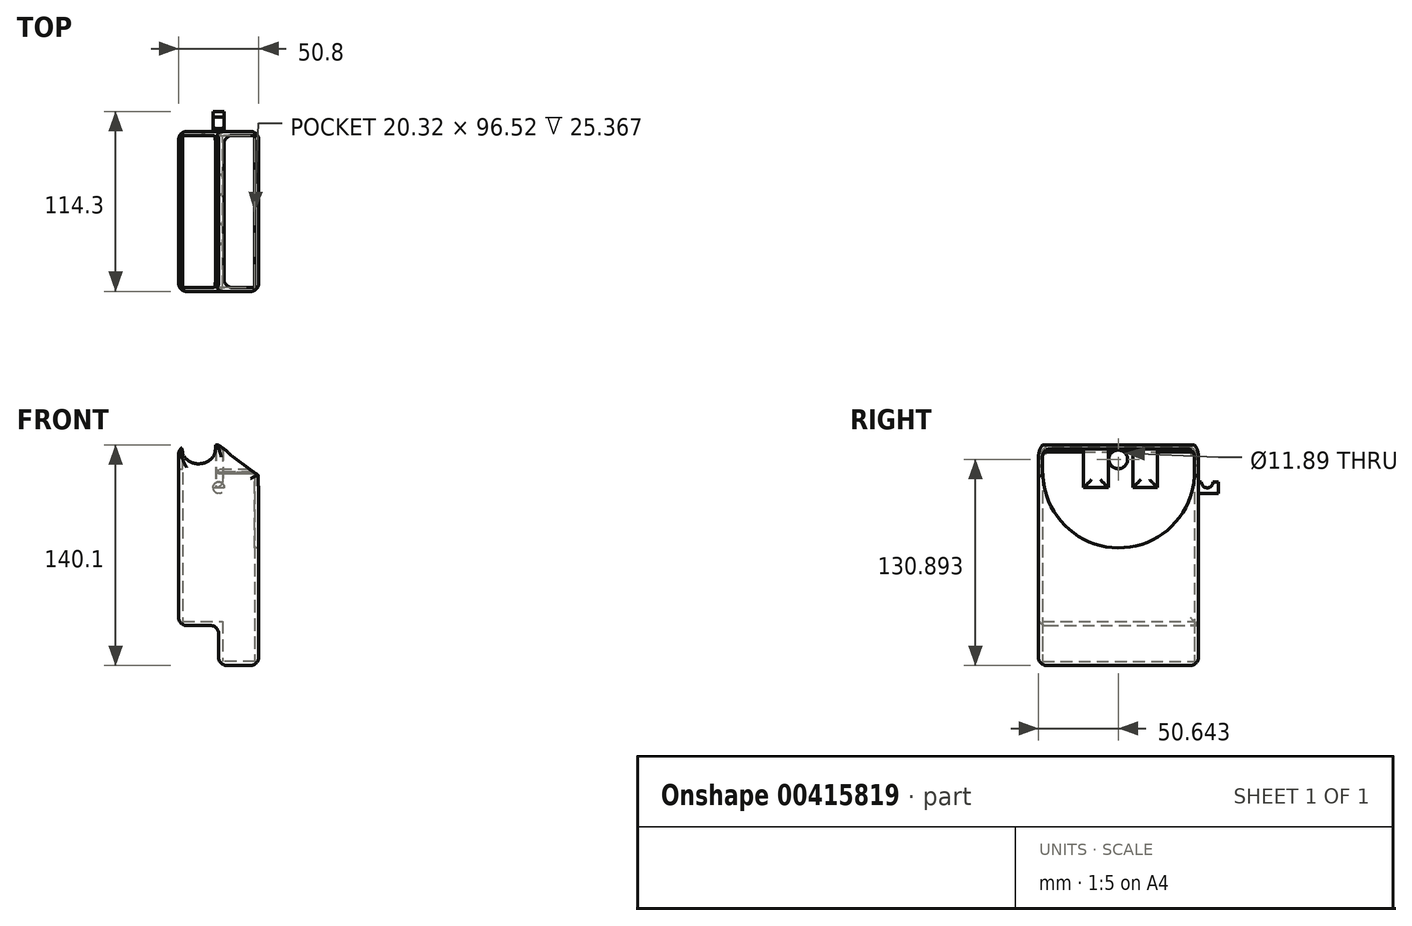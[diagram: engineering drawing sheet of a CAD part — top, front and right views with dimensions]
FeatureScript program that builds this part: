
annotation { "Feature Type Name" : "Feature", "Feature Type Description" : "" }
export const myFeature = defineFeature(function(context is Context, id is Id, definition is map)
    precondition{}
    {
        {
            var Q0;
            Q0=qCreatedBy(makeId("Front.planeOp"),FACE);
            var sketch = newSketch(context, id + "F0", { "sketchPlane" : qUnion([Q0])});
            skLineSegment(sketch, "E0", {"start": v(-25.4, 26.25) * mm, "end": v(-25.4, -87.62) * mm});
            skLineSegment(sketch, "E1", {"start": v(-25.4, -87.62) * mm, "end": v(0, -87.62) * mm});
            skLineSegment(sketch, "E2", {"start": v(0, 27.1) * mm, "end": v(0, -87.23) * mm});
            skLineSegment(sketch, "E3", {"start": v(25.4, -87.23) * mm, "end": v(25.4, 8.36) * mm});
            skLineSegment(sketch, "E4", {"start": v(0, 27.1) * mm, "end": v(25.4, 8.36) * mm});
            skLineSegment(sketch, "E5", {"start": v(-25.4, 26.25) * mm, "end": v(-23.58, 26.31) * mm});
            skArc(sketch, "E6", {"start": v(-23.58, 26.31) * mm, "mid": v(-12.33, 15.8) * mm, "end": v(-1.82, 27.05) * mm});
            skLineSegment(sketch, "E7.trimOffspring", {"start": v(-1.82, 27.05) * mm, "end": v(0, 27.1) * mm});
            skLineSegment(sketch, "E8", {"start": v(0, -87.23) * mm, "end": v(0, -112.99) * mm});
            skLineSegment(sketch, "E9", {"start": v(25.4, -87.23) * mm, "end": v(25.4, -112.99) * mm});
            skLineSegment(sketch, "E10", {"start": v(25.4, -112.99) * mm, "end": v(0, -112.99) * mm});
            skSolve(sketch);
        }
        {
            var Q0;
            Q0 = qSketchRegion(id + "F0", true);
            extrude(context, id + "F1", {"entities" : qUnion([Q0]), "depth" : 101.6 * mm});
        }
        {
            var Q0;
            Q0=makeQuery(id+"F1.opExtrude","SWEPT_FACE",FACE,{"disambiguationData":[OSD([sQuery(id+"F0.wireOp",EDGE,"E4")])]});
            var Q1;
            Q1=makeQuery(id+"F1.opExtrude","SWEPT_FACE",FACE,{"disambiguationData":[OSD([sQuery(id+"F0.wireOp",EDGE,"E6")])]});
            shell(context, id + "F2", {"entities" : qUnion([Q0, Q1]), "thickness" : 2.54 * mm});
        }
        {
            var Q0;
            Q0=qCreatedBy(makeId("Right.planeOp"),FACE);
            var sketch = newSketch(context, id + "F3", { "sketchPlane" : qUnion([Q0])});
            skArc(sketch, "E11", {"start": v(-98.82, 9.51) * mm, "mid": v(-50.48, -38.25) * mm, "end": v(-2.52, 9.9) * mm});
            skLineSegment(sketch, "E12", {"start": v(-98.82, 9.51) * mm, "end": v(-50.67, 9.9) * mm});
            skLineSegment(sketch, "E13", {"start": v(-2.52, 9.9) * mm, "end": v(-50.67, 9.9) * mm});
            skSolve(sketch);
        }
        {
            var Q0;
            Q0 = qSketchRegion(id + "F3", true);
            extrude(context, id + "F4", {"entities" : qUnion([Q0]), "operationType" : NewBodyOperationType.REMOVE, "depth" : 25.4 * mm});
        }
        {
            var Q0;
            Q0=qCreatedBy(makeId("Right.planeOp"),FACE);
            var sketch = newSketch(context, id + "F5", { "sketchPlane" : qUnion([Q0])});
            skCircle(sketch, "E14", {"center": v(-50.96, 17.9) * mm, "radius": 5.95 * mm});
            skSolve(sketch);
        }
        {
            var Q0;
            Q0 = qSketchRegion(id + "F5", true);
            extrude(context, id + "F6", {"entities" : qUnion([Q0]), "operationType" : NewBodyOperationType.REMOVE, "oppositeDirection" : true, "depth" : 25.4 * mm});
        }
        {
            var Q0;
            Q0=qCreatedBy(makeId("Front.planeOp"),FACE);
            var sketch = newSketch(context, id + "F7", { "sketchPlane" : qUnion([Q0])});
            skCircle(sketch, "E15", {"center": v(0, 0) * mm, "radius": 3.57 * mm});
            skSolve(sketch);
        }
        {
            var Q0;
            Q0 = qSketchRegion(id + "F7", true);
            extrude(context, id + "F8", {"entities" : qUnion([Q0]), "operationType" : NewBodyOperationType.ADD, "oppositeDirection" : true, "depth" : 12.7 * mm});
        }
        {
            var Q0;
            Q0=qCreatedBy(makeId("Right.planeOp"),FACE);
            var sketch = newSketch(context, id + "F9", { "sketchPlane" : qUnion([Q0])});
            skCircle(sketch, "E16", {"center": v(5.6, 3.45) * mm, "radius": 3.64 * mm});
            skSolve(sketch);
        }
        {
            var Q0;
            Q0 = qSketchRegion(id + "F9", true);
            extrude(context, id + "F10", {"entities" : qUnion([Q0]), "operationType" : NewBodyOperationType.REMOVE, "endBound" : BoundingType.SYMMETRIC, "depth" : 25.4 * mm});
        }
        {
            var Q0;
            Q0=makeQuery(id+"F1.opExtrude","CAP_EDGE",EDGE,{"disambiguationData":[OSD([sQuery(id+"F0.wireOp",EDGE,"E0")])],"isStart":true});
            var Q1;
            Q1=makeQuery(id+"F1.opExtrude","SWEPT_EDGE",EDGE,{"disambiguationData":[OSD([sQuery(id+"F0.wireOp",EDGE,"E0"),sQuery(id+"F0.wireOp",EDGE,"E1")])]});
            var Q2;
            Q2=makeQuery(id+"F1.opExtrude","CAP_EDGE",EDGE,{"disambiguationData":[OSD([sQuery(id+"F0.wireOp",EDGE,"E0")])],"isStart":false});
            var Q3;
            Q3=makeQuery(id+"F1.opExtrude","CAP_EDGE",EDGE,{"disambiguationData":[OSD([sQuery(id+"F0.wireOp",EDGE,"E1")])],"isStart":false});
            var Q4;
            Q4=makeQuery(id+"F1.opExtrude","CAP_EDGE",EDGE,{"disambiguationData":[OSD([sQuery(id+"F0.wireOp",EDGE,"E8")])],"isStart":false});
            var Q5;
            Q5=makeQuery(id+"F1.opExtrude","SWEPT_EDGE",EDGE,{"disambiguationData":[OSD([sQuery(id+"F0.wireOp",EDGE,"E8"),sQuery(id+"F0.wireOp",EDGE,"E10")])]});
            var Q6;
            Q6=makeQuery(id+"F1.opExtrude","SWEPT_FACE",FACE,{"disambiguationData":[OSD([sQuery(id+"F0.wireOp",EDGE,"E8")])]});
            var Q7;
            Q7=makeQuery(id+"F1.opExtrude","CAP_EDGE",EDGE,{"disambiguationData":[OSD([sQuery(id+"F0.wireOp",EDGE,"E10")])],"isStart":true});
            var Q8;
            Q8=makeQuery(id+"F1.opExtrude","CAP_EDGE",EDGE,{"disambiguationData":[OSD([sQuery(id+"F0.wireOp",EDGE,"E3"),sQuery(id+"F0.wireOp",EDGE,"E9")])],"isStart":true});
            var Q9;
            Q9=makeQuery(id+"F1.opExtrude","SWEPT_EDGE",EDGE,{"disambiguationData":[OSD([sQuery(id+"F0.wireOp",EDGE,"E9"),sQuery(id+"F0.wireOp",EDGE,"E10")])]});
            var Q10;
            Q10=makeQuery(id+"F1.opExtrude","CAP_EDGE",EDGE,{"disambiguationData":[OSD([sQuery(id+"F0.wireOp",EDGE,"E3"),sQuery(id+"F0.wireOp",EDGE,"E9")])],"isStart":false});
            var Q11;
            Q11=makeQuery(id+"F1.opExtrude","CAP_EDGE",EDGE,{"disambiguationData":[OSD([sQuery(id+"F0.wireOp",EDGE,"E10")])],"isStart":false});
            var Q12;
            Q12=makeQuery(id+"F1.opExtrude","CAP_EDGE",EDGE,{"disambiguationData":[OSD([sQuery(id+"F0.wireOp",EDGE,"E6")])],"isStart":true});
            var Q13;
            Q13=makeQuery(id+"F1.opExtrude","CAP_EDGE",EDGE,{"disambiguationData":[OSD([sQuery(id+"F0.wireOp",EDGE,"E6")])],"isStart":false});
            var Q14;
            Q14=makeQuery(id+"F1.opExtrude","CAP_EDGE",EDGE,{"disambiguationData":[OSD([sQuery(id+"F0.wireOp",EDGE,"E4")])],"isStart":false});
            fillet(context, id + "F11", {"entities" : qUnion([Q0, Q1, Q2, Q3, Q4, Q5, Q6, Q7, Q8, Q9, Q10, Q11, Q12, Q13, Q14]), "radius" : 5.08 * mm, "tangentPropagation" : true, "allowEdgeOverflow" : false});
        }
        {
            var Q0;
            Q0=qCreatedBy(makeId("Right.planeOp"),FACE);
            var sketch = newSketch(context, id + "F12", { "sketchPlane" : qUnion([Q0])});
            skLineSegment(sketch, "E17.bottom", {"start": v(-98.06, 11.65) * mm, "end": v(-2.9, 11.65) * mm});
            skLineSegment(sketch, "E17.top", {"start": v(-98.06, 9) * mm, "end": v(-2.9, 9) * mm});
            skLineSegment(sketch, "E17.right", {"start": v(-2.9, 11.65) * mm, "end": v(-2.9, 9) * mm});
            skLineSegment(sketch, "E18.bottom", {"start": v(-98.06, 9) * mm, "end": v(-99.13, 9) * mm});
            skLineSegment(sketch, "E18.top", {"start": v(-98.06, 11.65) * mm, "end": v(-99.13, 11.65) * mm});
            skLineSegment(sketch, "E18.right", {"start": v(-99.13, 9) * mm, "end": v(-99.13, 11.65) * mm});
            skLineSegment(sketch, "E19", {"start": v(-99.13, 11.65) * mm, "end": v(-99.13, 9) * mm});
            skSolve(sketch);
        }
        {
            var Q0;
            Q0 = qSketchRegion(id + "F12", true);
            extrude(context, id + "F13", {"entities" : qUnion([Q0]), "operationType" : NewBodyOperationType.REMOVE, "depth" : 25.4 * mm});
        }
        {
            var Q0;
            {var subQ0=sQuery(id+"F0.wireOp",EDGE,"E7.trimOffspring");Q0=makeQuery(id+"F2.opShell","OFFSET_EDGE",EDGE,{"disambiguationData":[OSD([subQ0]),TDD([makeQuery(id+"F1.opExtrude","CAP_EDGE",EDGE,{"disambiguationData":[OSD([subQ0])],"isStart":true})])]});}
            var Q1;
            {var subQ0=sQuery(id+"F0.wireOp",EDGE,"E7.trimOffspring");Q1=makeQuery(id+"F2.opShell","OFFSET_EDGE",EDGE,{"disambiguationData":[OSD([subQ0]),TDD([makeQuery(id+"F1.opExtrude","CAP_EDGE",EDGE,{"disambiguationData":[OSD([subQ0])],"isStart":false})])]});}
            fillet(context, id + "F14", {"entities" : qUnion([Q0, Q1]), "radius" : 5.08 * mm, "tangentPropagation" : true, "allowEdgeOverflow" : false});
        }
        {
            var Q0;
            Q0=makeQuery(id+"F1.opExtrude","SWEPT_EDGE",EDGE,{"disambiguationData":[OSD([sQuery(id+"F0.wireOp",EDGE,"E0"),sQuery(id+"F0.wireOp",EDGE,"E5")])]});
            fillet(context, id + "F15", {"entities" : qUnion([Q0]), "radius" : 5.08 * mm, "tangentPropagation" : true, "allowEdgeOverflow" : false});
        }
        {
            var Q0;
            Q0=qCreatedBy(makeId("Top.planeOp"),FACE);
            var sketch = newSketch(context, id + "F16", { "sketchPlane" : qUnion([Q0])});
            skLineSegment(sketch, "E20", {"start": v(-1.67, -25.96) * mm, "end": v(2.84, -25.96) * mm});
            skLineSegment(sketch, "E21", {"start": v(2.84, -25.96) * mm, "end": v(2.84, -41.63) * mm});
            skLineSegment(sketch, "E22", {"start": v(2.84, -41.63) * mm, "end": v(-1.82, -41.63) * mm});
            skLineSegment(sketch, "E23", {"start": v(-1.82, -41.63) * mm, "end": v(-1.67, -25.96) * mm});
            skLineSegment(sketch, "E24.MirrorCS", {"start": v(-1.67, -57.3) * mm, "end": v(2.84, -57.3) * mm});
            skPoint(sketch, "E25.MirrorCS.end.orphan", {"position": v(7.36, -57.3) * mm});
            skPoint(sketch, "E25.MirrorCS.start.orphan", {"position": v(7.5, -41.63) * mm});
            skPoint(sketch, "E26.MirrorCS.end.orphan", {"position": v(2.84, -57.3) * mm});
            skLineSegment(sketch, "E27.MirrorCS", {"start": v(-1.82, -72.97) * mm, "end": v(-1.67, -57.3) * mm});
            skLineSegment(sketch, "E28.MirrorCS", {"start": v(2.84, -57.3) * mm, "end": v(2.84, -72.97) * mm});
            skLineSegment(sketch, "E29.MirrorCS", {"start": v(2.84, -72.97) * mm, "end": v(-1.82, -72.97) * mm});
            skPoint(sketch, "E30.MirrorCS.end.orphan", {"position": v(2.84, -41.63) * mm});
            skPoint(sketch, "E31.MirrorCS.end.orphan", {"position": v(-1.67, -57.3) * mm});
            skPoint(sketch, "E31.MirrorCS.start.orphan", {"position": v(-1.82, -41.63) * mm});
            skSolve(sketch);
        }
        {
            var Q0;
            Q0 = qSketchRegion(id + "F16", true);
            extrude(context, id + "F17", {"entities" : qUnion([Q0]), "operationType" : NewBodyOperationType.ADD, "depth" : 24.9 * mm});
        }
        {
            var Q0;
            Q0=makeQuery(id+"F17.opExtrude","SWEPT_EDGE",EDGE,{"disambiguationData":[OSD([sQuery(id+"F16.wireOp",EDGE,"E21"),sQuery(id+"F16.wireOp",EDGE,"E20")])]});
            var Q1;
            Q1=makeQuery(id+"F17.opExtrude","SWEPT_EDGE",EDGE,{"disambiguationData":[OSD([sQuery(id+"F16.wireOp",EDGE,"E22"),sQuery(id+"F16.wireOp",EDGE,"E21")])]});
            var Q2;
            Q2=makeQuery(id+"F17.opExtrude","CAP_EDGE",EDGE,{"disambiguationData":[OSD([sQuery(id+"F16.wireOp",EDGE,"E21")])],"isStart":true});
            var Q3;
            Q3=makeQuery(id+"F17.opExtrude","SWEPT_EDGE",EDGE,{"disambiguationData":[OSD([sQuery(id+"F16.wireOp",EDGE,"E24.MirrorCS"),sQuery(id+"F16.wireOp",EDGE,"E28.MirrorCS")])]});
            var Q4;
            Q4=makeQuery(id+"F17.opExtrude","SWEPT_EDGE",EDGE,{"disambiguationData":[OSD([sQuery(id+"F16.wireOp",EDGE,"E28.MirrorCS"),sQuery(id+"F16.wireOp",EDGE,"E29.MirrorCS")])]});
            var Q5;
            Q5=makeQuery(id+"F17.opExtrude","CAP_EDGE",EDGE,{"disambiguationData":[OSD([sQuery(id+"F16.wireOp",EDGE,"E28.MirrorCS")])],"isStart":true});
            fillet(context, id + "F18", {"entities" : qUnion([Q0, Q1, Q2, Q3, Q4, Q5]), "radius" : 5.08 * mm, "tangentPropagation" : true, "allowEdgeOverflow" : false});
        }
        {
            var Q0;
            Q0=makeQuery(id+"F1.opExtrude","CAP_EDGE",EDGE,{"disambiguationData":[OSD([sQuery(id+"F0.wireOp",EDGE,"E4")])],"isStart":true});
            fillet(context, id + "F19", {"entities" : qUnion([Q0]), "radius" : 5.08 * mm, "allowEdgeOverflow" : false});
        }
    });
